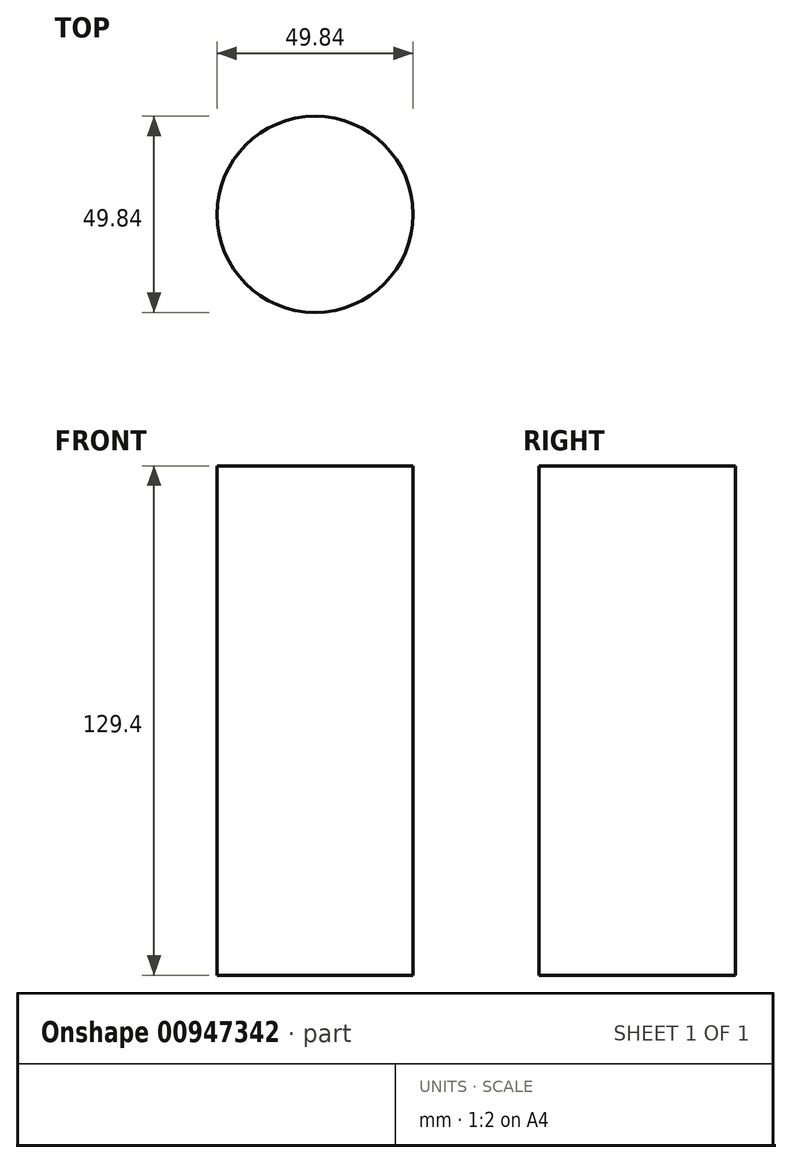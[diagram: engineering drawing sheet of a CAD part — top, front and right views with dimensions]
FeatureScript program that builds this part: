
annotation { "Feature Type Name" : "Feature", "Feature Type Description" : "" }
export const myFeature = defineFeature(function(context is Context, id is Id, definition is map)
    precondition{}
    {
        {
            var Q0;
            Q0=qCreatedBy(makeId("Top.planeOp"),FACE);
            var sketch = newSketch(context, id + "F0", { "sketchPlane" : qUnion([Q0])});
            skCircle(sketch, "E0", {"center": v(15.18, 0) * mm, "radius": 24.92 * mm});
            skSolve(sketch);
        }
        {
            var Q0;
            Q0=makeQuery(id+"F0.imprint","IMPRINT",FACE,{"disambiguationData":[TD([[makeQuery(id+"F0.imprint","IMPRINT",EDGE,{"derivedFrom":sQuery(id+"F0.wireOp",EDGE,"E0")}),1.0]])]});
            extrude(context, id + "F1", {"entities" : qUnion([Q0]), "depth" : 129.4 * mm, "offsetDistance" : 25.4 * mm});
        }
    });
